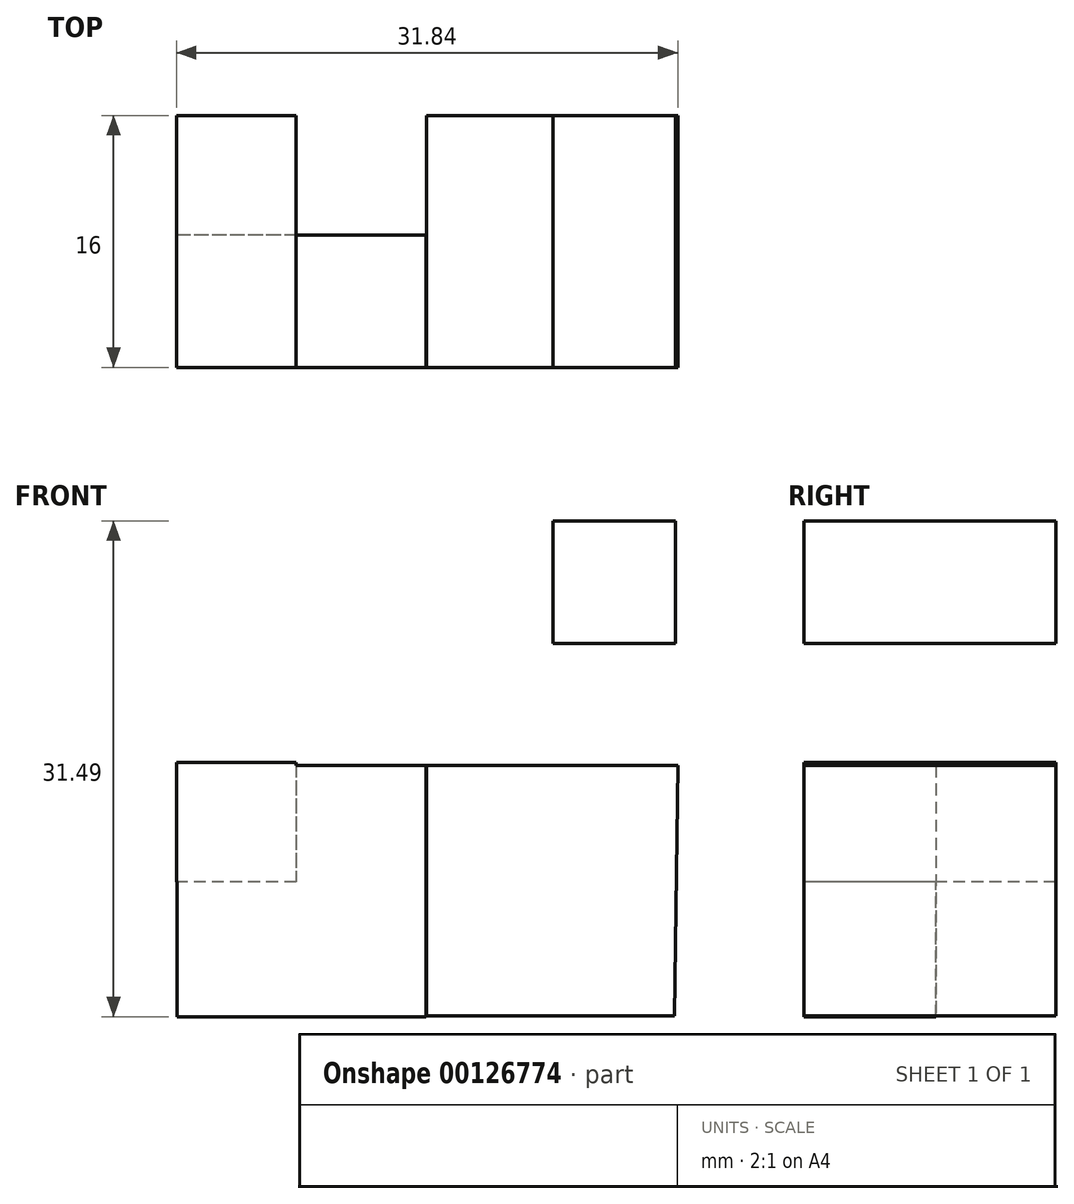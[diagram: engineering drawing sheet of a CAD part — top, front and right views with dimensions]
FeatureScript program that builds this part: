
annotation { "Feature Type Name" : "Feature", "Feature Type Description" : "" }
export const myFeature = defineFeature(function(context is Context, id is Id, definition is map)
    precondition{}
    {
        {
            var Q0;
            Q0=qCreatedBy(makeId("Front.planeOp"),FACE);
            var sketch = newSketch(context, id + "F0", { "sketchPlane" : qUnion([Q0])});
            skLineSegment(sketch, "E0", {"start": v(14.7, 23.49) * mm, "end": v(14.7, -8.1) * mm});
            skLineSegment(sketch, "E1", {"start": v(14.7, -8.1) * mm, "end": v(-16.9, -8.1) * mm});
            skLineSegment(sketch, "E2", {"start": v(-16.9, -8.1) * mm, "end": v(-16.9, 7.9) * mm});
            skLineSegment(sketch, "E3", {"start": v(-16.9, 7.9) * mm, "end": v(6.92, 7.9) * mm});
            skLineSegment(sketch, "E4", {"start": v(6.92, 7.9) * mm, "end": v(6.92, 23.49) * mm});
            skLineSegment(sketch, "E5", {"start": v(14.7, 23.49) * mm, "end": v(6.92, 23.49) * mm});
            skSolve(sketch);
        }
        {
            var Q0;
            Q0=makeQuery(id+"F0.imprint","IMPRINT",FACE,{"disambiguationData":[TD([[makeQuery(id+"F0.imprint","IMPRINT",EDGE,{"derivedFrom":sQuery(id+"F0.wireOp",EDGE,"E0")}),-1.0]])]});
            var sketch = newSketch(context, id + "F1", { "sketchPlane" : qUnion([Q0])});
            skLineSegment(sketch, "E6", {"start": v(14.58, 23.55) * mm, "end": v(6.8, 23.55) * mm});
            skLineSegment(sketch, "E7", {"start": v(14.58, 23.55) * mm, "end": v(14.58, 15.77) * mm});
            skLineSegment(sketch, "E8", {"start": v(14.58, 15.77) * mm, "end": v(6.8, 15.77) * mm});
            skLineSegment(sketch, "E9", {"start": v(6.8, 23.55) * mm, "end": v(6.8, 15.77) * mm});
            skLineSegment(sketch, "E10", {"start": v(14.49, -7.89) * mm, "end": v(-1.26, -7.89) * mm});
            skLineSegment(sketch, "E11", {"start": v(-1.26, -7.89) * mm, "end": v(-1.26, 8.03) * mm});
            skLineSegment(sketch, "E12", {"start": v(-1.26, 8.03) * mm, "end": v(14.71, 8.03) * mm});
            skLineSegment(sketch, "E13", {"start": v(14.71, 8.03) * mm, "end": v(14.49, -7.89) * mm});
            skLineSegment(sketch, "E14", {"start": v(-1.26, 0) * mm, "end": v(-1.26, -7.89) * mm});
            skSolve(sketch);
        }
        {
            var Q0;
            Q0 = qSketchRegion(id + "F1", true);
            extrude(context, id + "F2", {"entities" : qUnion([Q0]), "oppositeDirection" : true, "depth" : 16 * mm});
        }
        {
            var Q0;
            Q0=makeQuery(id+"F0.imprint","IMPRINT",FACE,{"disambiguationData":[TD([[makeQuery(id+"F0.imprint","IMPRINT",EDGE,{"derivedFrom":sQuery(id+"F0.wireOp",EDGE,"E0")}),-1.0]])]});
            var sketch = newSketch(context, id + "F3", { "sketchPlane" : qUnion([Q0])});
            skLineSegment(sketch, "E15", {"start": v(-17.1, 8.01) * mm, "end": v(-1.3, 8.01) * mm});
            skLineSegment(sketch, "E16", {"start": v(-1.3, 8.01) * mm, "end": v(-1.3, -7.94) * mm});
            skLineSegment(sketch, "E17", {"start": v(-1.3, -7.94) * mm, "end": v(-17.1, -7.94) * mm});
            skLineSegment(sketch, "E18", {"start": v(-17.1, -7.94) * mm, "end": v(-17.1, 8.01) * mm});
            skSolve(sketch);
        }
        {
            var Q0;
            Q0 = qSketchRegion(id + "F3", true);
            extrude(context, id + "F4", {"entities" : qUnion([Q0]), "oppositeDirection" : true, "depth" : 8.4 * mm});
        }
        {
            var Q0;
            Q0=makeQuery(id+"F0.imprint","IMPRINT",FACE,{"disambiguationData":[TD([[makeQuery(id+"F0.imprint","IMPRINT",EDGE,{"derivedFrom":sQuery(id+"F0.wireOp",EDGE,"E0")}),-1.0]])]});
            var sketch = newSketch(context, id + "F5", { "sketchPlane" : qUnion([Q0])});
            skLineSegment(sketch, "E19", {"start": v(-17.13, 8.21) * mm, "end": v(-9.53, 8.21) * mm});
            skLineSegment(sketch, "E20", {"start": v(-9.53, 8.21) * mm, "end": v(-9.53, 0.61) * mm});
            skLineSegment(sketch, "E21", {"start": v(-9.53, 0.61) * mm, "end": v(-17.13, 0.61) * mm});
            skLineSegment(sketch, "E22", {"start": v(-17.13, 0.61) * mm, "end": v(-17.13, 8.21) * mm});
            skSolve(sketch);
        }
        {
            var Q0;
            Q0 = qSketchRegion(id + "F5", true);
            extrude(context, id + "F6", {"entities" : qUnion([Q0]), "operationType" : NewBodyOperationType.ADD, "oppositeDirection" : true, "depth" : 16 * mm});
        }
    });
